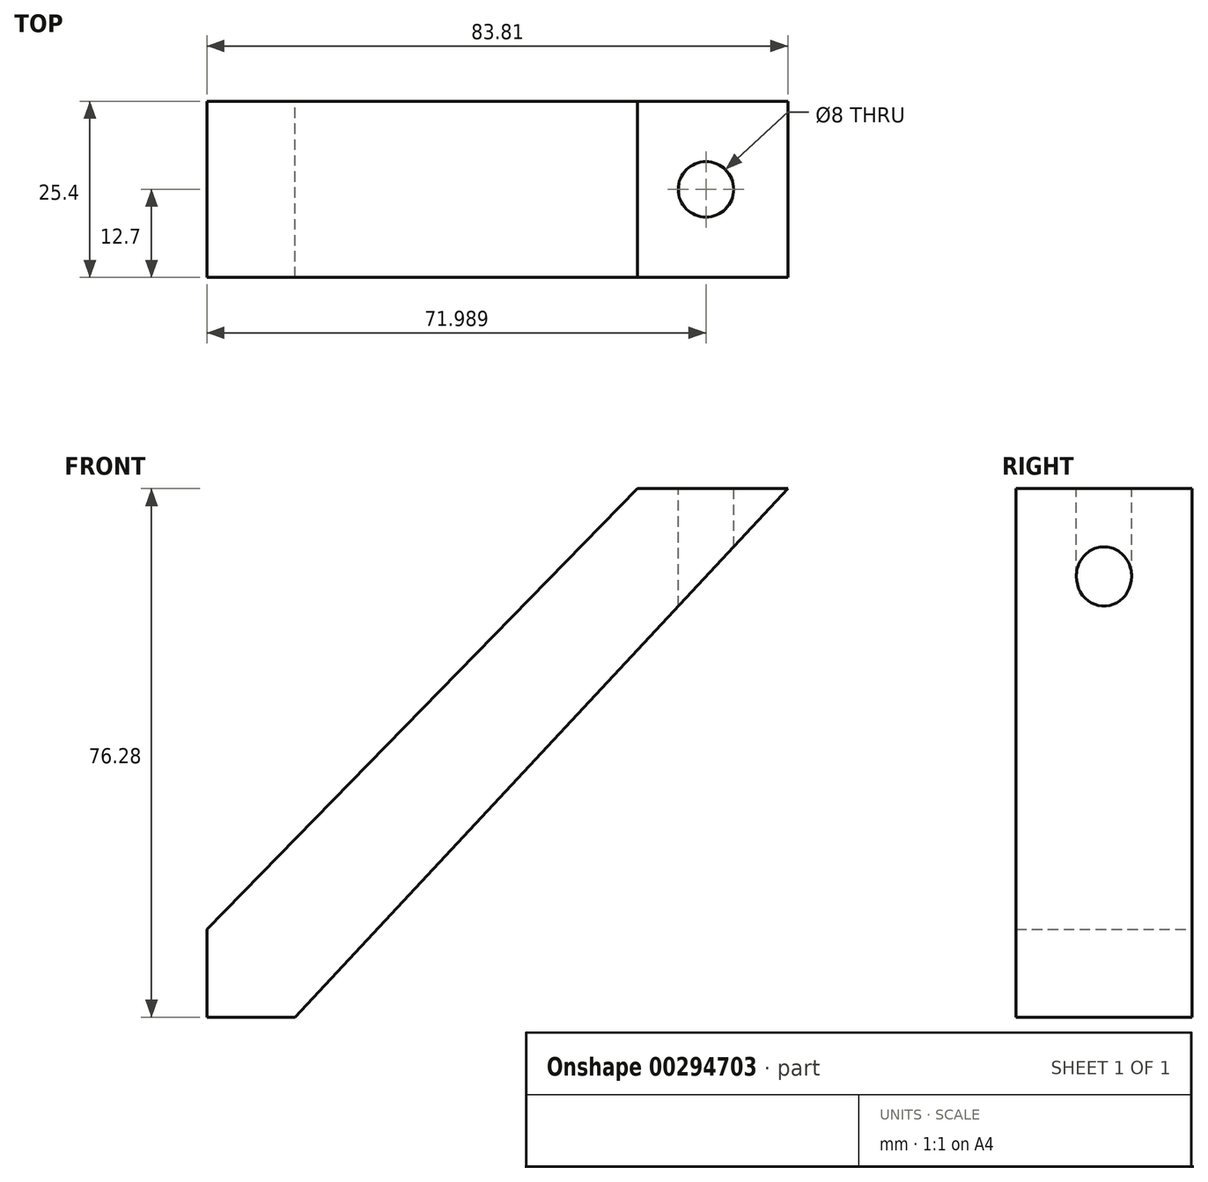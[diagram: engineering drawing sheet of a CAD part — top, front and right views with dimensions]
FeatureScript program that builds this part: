
annotation { "Feature Type Name" : "Feature", "Feature Type Description" : "" }
export const myFeature = defineFeature(function(context is Context, id is Id, definition is map)
    precondition{}
    {
        {
            var Q0;
            Q0=qCreatedBy(makeId("Front.planeOp"),FACE);
            var sketch = newSketch(context, id + "F0", { "sketchPlane" : qUnion([Q0])});
            skLineSegment(sketch, "E0", {"start": v(-37.33, -37.95) * mm, "end": v(-37.33, -25.25) * mm});
            skLineSegment(sketch, "E1", {"start": v(-37.33, -37.95) * mm, "end": v(-24.63, -37.95) * mm});
            skLineSegment(sketch, "E2", {"start": v(-37.33, -25.25) * mm, "end": v(24.8, 38.33) * mm});
            skLineSegment(sketch, "E3", {"start": v(-24.63, -37.95) * mm, "end": v(46.48, 38.33) * mm});
            skLineSegment(sketch, "E4", {"start": v(24.8, 38.33) * mm, "end": v(46.48, 38.33) * mm});
            skSolve(sketch);
        }
        {
            var Q0;
            Q0 = qSketchRegion(id + "F0", true);
            extrude(context, id + "F1", {"entities" : qUnion([Q0]), "endBound" : BoundingType.SYMMETRIC, "depth" : 25.4 * mm});
        }
        {
            var Q0;
            Q0=makeQuery(id+"F1.opExtrude","SWEPT_FACE",FACE,{"disambiguationData":[OSD([sQuery(id+"F0.wireOp",EDGE,"E4")])]});
            var sketch = newSketch(context, id + "F2", { "sketchPlane" : qUnion([Q0])});
            skCircle(sketch, "E5", {"center": v(34.66, 0) * mm, "radius": 4 * mm});
            skSolve(sketch);
        }
        {
            var Q0;
            Q0 = qSketchRegion(id + "F2", true);
            extrude(context, id + "F3", {"entities" : qUnion([Q0]), "operationType" : NewBodyOperationType.REMOVE, "oppositeDirection" : true, "depth" : 25.4 * mm});
        }
    });
